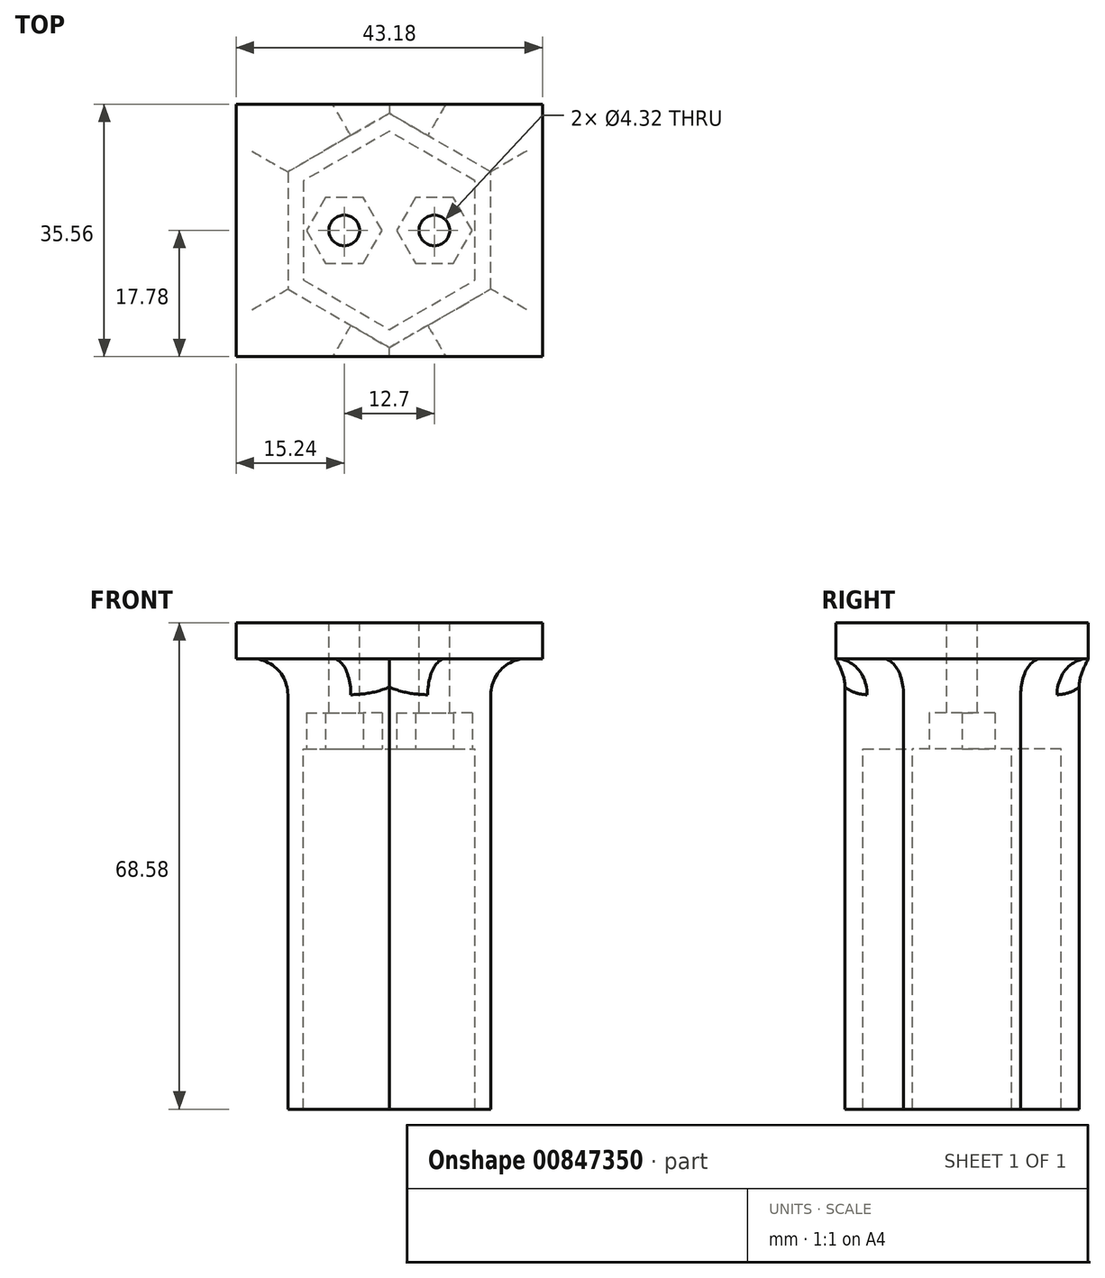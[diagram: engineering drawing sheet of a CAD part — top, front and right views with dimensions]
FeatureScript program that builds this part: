
annotation { "Feature Type Name" : "Feature", "Feature Type Description" : "" }
export const myFeature = defineFeature(function(context is Context, id is Id, definition is map)
    precondition{}
    {
        {
            var Q0;
            Q0=qCreatedBy(makeId("Front.planeOp"),FACE);
            var sketch = newSketch(context, id + "F0", { "sketchPlane" : qUnion([Q0])});
            skLineSegment(sketch, "E0.bottom", {"start": v(-21.6, 33.81) * mm, "end": v(21.6, 33.81) * mm});
            skLineSegment(sketch, "E0.left", {"start": v(-21.59, 33.81) * mm, "end": v(-21.59, 28.73) * mm});
            skLineSegment(sketch, "E0.right", {"start": v(21.6, 33.81) * mm, "end": v(21.6, 28.73) * mm});
            skPoint(sketch, "E0.middle", {"position": v(0, 31.27) * mm});
            skLineSegment(sketch, "E1", {"start": v(21.6, 28.73) * mm, "end": v(-21.59, 28.73) * mm});
            skSolve(sketch);
        }
        {
            var Q0;
            Q0=makeQuery(id+"F0.imprint","IMPRINT",FACE,{"disambiguationData":[TD([[makeQuery(id+"F0.imprint","IMPRINT",EDGE,{"derivedFrom":sQuery(id+"F0.wireOp",EDGE,"E0.bottom")}),-1.0]])]});
            extrude(context, id + "F1", {"entities" : qUnion([Q0]), "endBound" : BoundingType.SYMMETRIC, "depth" : 35.56 * mm, "offsetDistance" : 25.4 * mm});
        }
        {
            var Q0;
            Q0=makeQuery(id+"F1.opExtrude","SWEPT_FACE",FACE,{"disambiguationData":[OSD([sQuery(id+"F0.wireOp",EDGE,"E0.bottom")])]});
            var sketch = newSketch(context, id + "F2", { "sketchPlane" : qUnion([Q0])});
            skCircle(sketch, "E2", {"center": v(-6.35, 0) * mm, "radius": 2.16 * mm});
            skCircle(sketch, "E3", {"center": v(6.35, 0) * mm, "radius": 2.16 * mm});
            skSolve(sketch);
        }
        {
            var Q0;
            Q0=makeQuery(id+"F2.imprint","IMPRINT",FACE,{"disambiguationData":[TD([[makeQuery(id+"F2.imprint","IMPRINT",EDGE,{"derivedFrom":sQuery(id+"F2.wireOp",EDGE,"E2")}),1.0]])]});
            var Q1;
            Q1=makeQuery(id+"F2.imprint","IMPRINT",FACE,{"disambiguationData":[TD([[makeQuery(id+"F2.imprint","IMPRINT",EDGE,{"derivedFrom":sQuery(id+"F2.wireOp",EDGE,"E3")}),1.0]])]});
            extrude(context, id + "F3", {"entities" : qUnion([Q0, Q1]), "operationType" : NewBodyOperationType.REMOVE, "oppositeDirection" : true, "depth" : 25.4 * mm, "offsetDistance" : 25.4 * mm});
        }
        {
            var Q0;
            Q0=makeQuery(id+"F1.opExtrude","SWEPT_FACE",FACE,{"disambiguationData":[OSD([sQuery(id+"F0.wireOp",EDGE,"E1")])]});
            var sketch = newSketch(context, id + "F4", { "sketchPlane" : qUnion([Q0])});
            skCircle(sketch, "E4", {"center": v(0, 0) * mm, "radius": 16.51 * mm, "construction": true});
            skLineSegment(sketch, "E5.0", {"start": v(0, 16.51) * mm, "end": v(14.3, 8.25) * mm});
            skLineSegment(sketch, "E5.1", {"start": v(14.3, 8.25) * mm, "end": v(14.3, -8.26) * mm});
            skLineSegment(sketch, "E5.2", {"start": v(14.3, -8.26) * mm, "end": v(0, -16.51) * mm});
            skLineSegment(sketch, "E5.3", {"start": v(0, -16.51) * mm, "end": v(-14.3, -8.25) * mm});
            skLineSegment(sketch, "E5.4", {"start": v(-14.3, -8.26) * mm, "end": v(-14.3, 8.26) * mm});
            skLineSegment(sketch, "E5.5", {"start": v(-14.3, 8.26) * mm, "end": v(0, 16.5) * mm});
            skCircle(sketch, "E6", {"center": v(0, 0) * mm, "radius": 13.97 * mm, "construction": true});
            skLineSegment(sketch, "E7.0", {"start": v(0, 13.97) * mm, "end": v(12.1, 6.98) * mm});
            skLineSegment(sketch, "E7.1", {"start": v(12.1, 6.99) * mm, "end": v(12.1, -6.99) * mm});
            skLineSegment(sketch, "E7.2", {"start": v(12.1, -6.99) * mm, "end": v(0, -13.97) * mm});
            skLineSegment(sketch, "E7.3", {"start": v(0, -13.97) * mm, "end": v(-12.1, -6.98) * mm});
            skLineSegment(sketch, "E7.4", {"start": v(-12.1, -6.99) * mm, "end": v(-12.1, 6.99) * mm});
            skLineSegment(sketch, "E7.5", {"start": v(-12.1, 6.99) * mm, "end": v(0, 13.97) * mm});
            skSolve(sketch);
        }
        {
            var Q0;
            Q0=makeQuery(id+"F4.imprint","IMPRINT",FACE,{"disambiguationData":[TD([[makeQuery(id+"F4.imprint","IMPRINT",EDGE,{"derivedFrom":sQuery(id+"F4.wireOp",EDGE,"E5.0")}),-1.0]])]});
            extrude(context, id + "F5", {"entities" : qUnion([Q0]), "operationType" : NewBodyOperationType.ADD, "depth" : 63.5 * mm, "offsetDistance" : 25.4 * mm});
        }
        {
            var Q0;
            Q0=makeQuery(id+"F5.opExtrude","CAP_EDGE",EDGE,{"disambiguationData":[OSD([sQuery(id+"F4.wireOp",EDGE,"E5.4")])],"isStart":true});
            var Q1;
            Q1=makeQuery(id+"F5.opExtrude","CAP_EDGE",EDGE,{"disambiguationData":[OSD([sQuery(id+"F4.wireOp",EDGE,"E5.3")])],"isStart":true});
            var Q2;
            Q2=makeQuery(id+"F5.opExtrude","CAP_EDGE",EDGE,{"disambiguationData":[OSD([sQuery(id+"F4.wireOp",EDGE,"E5.2")])],"isStart":true});
            var Q3;
            Q3=makeQuery(id+"F5.opExtrude","CAP_EDGE",EDGE,{"disambiguationData":[OSD([sQuery(id+"F4.wireOp",EDGE,"E5.1")])],"isStart":true});
            var Q4;
            Q4=makeQuery(id+"F5.opExtrude","CAP_EDGE",EDGE,{"disambiguationData":[OSD([sQuery(id+"F4.wireOp",EDGE,"E5.0")])],"isStart":true});
            var Q5;
            Q5=makeQuery(id+"F5.opExtrude","CAP_EDGE",EDGE,{"disambiguationData":[OSD([sQuery(id+"F4.wireOp",EDGE,"E5.5")])],"isStart":true});
            fillet(context, id + "F6", {"entities" : qUnion([Q0, Q1, Q2, Q3, Q4, Q5]), "radius" : 5.08 * mm, "tangentPropagation" : true, "allowEdgeOverflow" : false});
        }
        {
            var Q0;
            {var subQ9=sQuery(id+"F4.wireOp",EDGE,"E7.0");Q0=makeQuery(id+"F4.imprint","IMPRINT",FACE,{"disambiguationData":[TD([[makeQuery(id+"F4.imprint","IMPRINT",EDGE,{"derivedFrom":subQ9}),-1.0]])]});}
            extrude(context, id + "F7", {"entities" : qUnion([Q0]), "operationType" : NewBodyOperationType.ADD, "depth" : 12.7 * mm, "offsetDistance" : 25.4 * mm});
        }
        {
            var Q0;
            Q0=makeQuery(id+"F7.opExtrude","CAP_FACE",FACE,{"disambiguationData":[OSD([sQuery(id+"F0.wireOp",EDGE,"E1"),sQuery(id+"F2.wireOp",EDGE,"E2"),sQuery(id+"F2.wireOp",EDGE,"E3"),sQuery(id+"F4.wireOp",EDGE,"E7.0"),sQuery(id+"F4.wireOp",EDGE,"E7.1"),sQuery(id+"F4.wireOp",EDGE,"E7.2"),sQuery(id+"F4.wireOp",EDGE,"E7.3"),sQuery(id+"F4.wireOp",EDGE,"E7.4"),sQuery(id+"F4.wireOp",EDGE,"E7.5")])],"isStart":false});
            var sketch = newSketch(context, id + "F8", { "sketchPlane" : qUnion([Q0])});
            skCircle(sketch, "E8.0", {"center": v(-6.35, 0) * mm, "radius": 2.16 * mm});
            skCircle(sketch, "E9.0", {"center": v(6.35, 0) * mm, "radius": 2.16 * mm});
            skCircle(sketch, "E10", {"center": v(-6.35, 0) * mm, "radius": 5.33 * mm, "construction": true});
            skLineSegment(sketch, "E11.0", {"start": v(-9.02, 4.62) * mm, "end": v(-3.68, 4.62) * mm});
            skLineSegment(sketch, "E11.1", {"start": v(-3.68, 4.62) * mm, "end": v(-1.02, 0) * mm});
            skLineSegment(sketch, "E11.2", {"start": v(-1.02, 0) * mm, "end": v(-3.68, -4.62) * mm});
            skLineSegment(sketch, "E11.3", {"start": v(-3.68, -4.62) * mm, "end": v(-9.02, -4.62) * mm});
            skLineSegment(sketch, "E11.4", {"start": v(-9.02, -4.62) * mm, "end": v(-11.68, 0) * mm});
            skLineSegment(sketch, "E11.5", {"start": v(-11.68, 0) * mm, "end": v(-9.02, 4.62) * mm});
            skCircle(sketch, "E12", {"center": v(6.35, 0) * mm, "radius": 5.33 * mm, "construction": true});
            skLineSegment(sketch, "E13.0", {"start": v(3.68, 4.62) * mm, "end": v(9.02, 4.62) * mm});
            skLineSegment(sketch, "E13.1", {"start": v(9.02, 4.62) * mm, "end": v(11.68, 0) * mm});
            skLineSegment(sketch, "E13.2", {"start": v(11.68, 0) * mm, "end": v(9.02, -4.62) * mm});
            skLineSegment(sketch, "E13.3", {"start": v(9.02, -4.62) * mm, "end": v(3.68, -4.62) * mm});
            skLineSegment(sketch, "E13.4", {"start": v(3.68, -4.62) * mm, "end": v(1.02, 0) * mm});
            skLineSegment(sketch, "E13.5", {"start": v(1.02, 0) * mm, "end": v(3.68, 4.62) * mm});
            skSolve(sketch);
        }
        {
            var Q0;
            Q0=makeQuery(id+"F8.imprint","IMPRINT",FACE,{"disambiguationData":[TD([[makeQuery(id+"F8.imprint","IMPRINT",EDGE,{"derivedFrom":sQuery(id+"F8.wireOp",EDGE,"E9.0")}),-1.0]])]});
            var Q1;
            Q1=makeQuery(id+"F8.imprint","IMPRINT",FACE,{"disambiguationData":[TD([[makeQuery(id+"F8.imprint","IMPRINT",EDGE,{"derivedFrom":sQuery(id+"F8.wireOp",EDGE,"E8.0")}),-1.0]])]});
            extrude(context, id + "F9", {"entities" : qUnion([Q0, Q1]), "operationType" : NewBodyOperationType.REMOVE, "oppositeDirection" : true, "depth" : 5.08 * mm, "offsetDistance" : 25.4 * mm});
        }
    });
